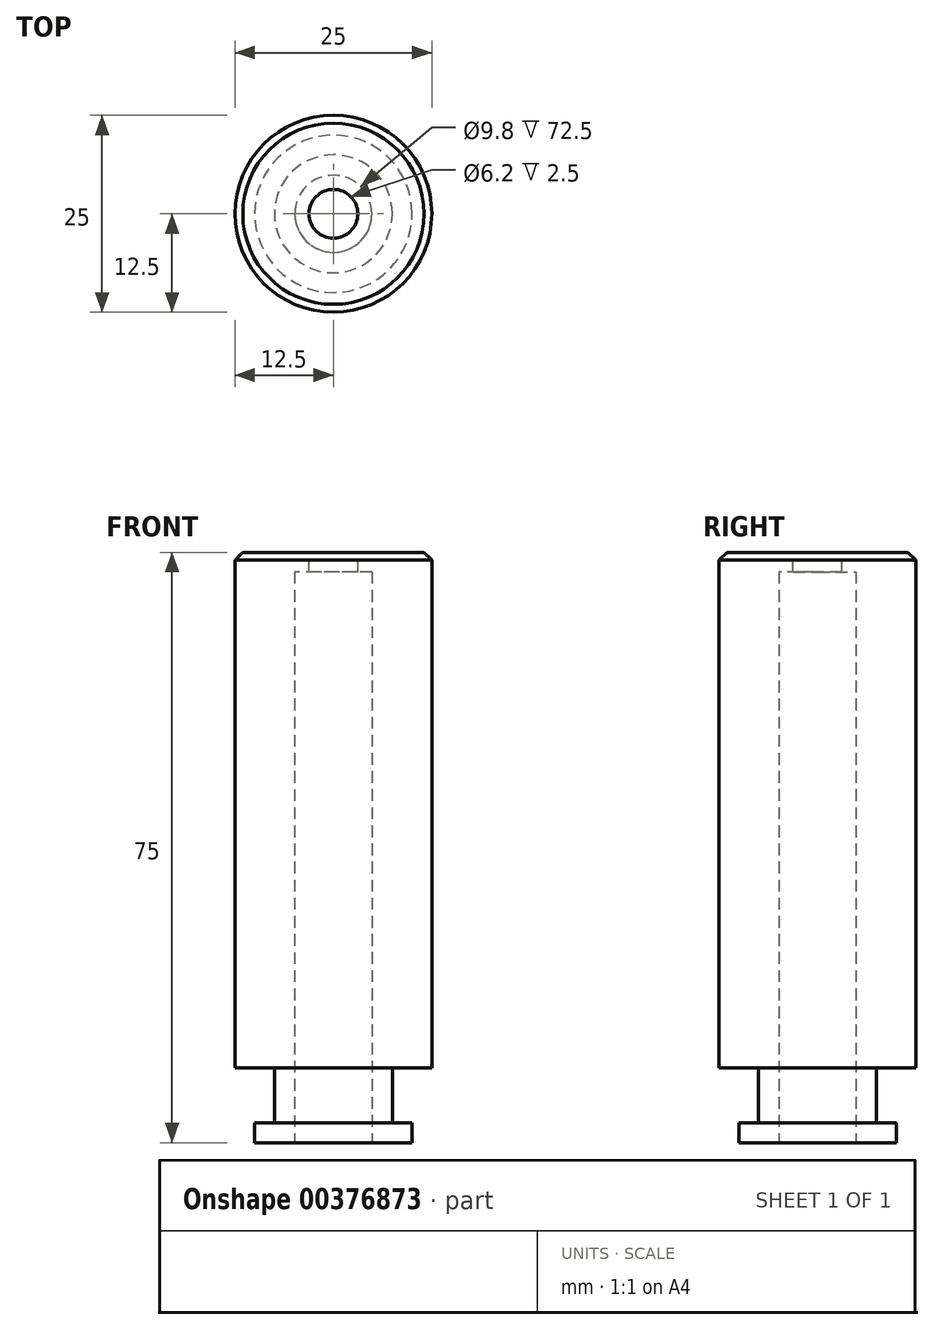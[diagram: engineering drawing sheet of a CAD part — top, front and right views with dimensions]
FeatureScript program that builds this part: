
annotation { "Feature Type Name" : "Feature", "Feature Type Description" : "" }
export const myFeature = defineFeature(function(context is Context, id is Id, definition is map)
    precondition{}
    {
        {
            var Q0;
            Q0=qCreatedBy(makeId("Top.planeOp"),FACE);
            var sketch = newSketch(context, id + "F0", { "sketchPlane" : qUnion([Q0])});
            skCircle(sketch, "E0", {"center": v(0, 0) * mm, "radius": 21.5 * mm});
            skSolve(sketch);
        }
        {
            var Q0;
            Q0=makeQuery(id+"F0.imprint","IMPRINT",FACE,{"disambiguationData":[TD([[makeQuery(id+"F0.imprint","IMPRINT",EDGE,{"derivedFrom":sQuery(id+"F0.wireOp",EDGE,"E0")}),1.0]])]});
            extrude(context, id + "F1", {"entities" : qUnion([Q0]), "depth" : 40 * mm});
        }
        {
            var Q0;
            Q0=makeQuery(id+"F1.opExtrude","CAP_EDGE",EDGE,{"disambiguationData":[OSD([sQuery(id+"F0.wireOp",EDGE,"E0")])],"isStart":false});
            fillet(context, id + "F2", {"entities" : qUnion([Q0]), "radius" : 5 * mm, "tangentPropagation" : true, "allowEdgeOverflow" : false});
        }
        {
            var Q0;
            Q0=makeQuery(id+"F1.opExtrude","CAP_FACE",FACE,{"disambiguationData":[OSD([sQuery(id+"F0.wireOp",EDGE,"E0")])],"isStart":true});
            var sketch = newSketch(context, id + "F3", { "sketchPlane" : qUnion([Q0])});
            skCircle(sketch, "E1", {"center": v(0, 0) * mm, "radius": 21.5 * mm});
            skSolve(sketch);
        }
        {
            var Q0;
            Q0=makeQuery(id+"F3.imprint","IMPRINT",FACE,{"disambiguationData":[TD([[makeQuery(id+"F3.imprint","IMPRINT",EDGE,{"derivedFrom":sQuery(id+"F3.wireOp",EDGE,"E1")}),-1.0]])]});
            extrude(context, id + "F4", {"entities" : qUnion([Q0]), "operationType" : NewBodyOperationType.ADD, "depth" : 40 * mm});
        }
        {
            var Q0;
            Q0=makeQuery(id+"F4.opExtrude","CAP_EDGE",EDGE,{"disambiguationData":[OSD([sQuery(id+"F3.wireOp",EDGE,"E1")])],"isStart":false});
            chamfer(context, id + "F5", {"entities" : qUnion([Q0]), "chamferType" : ChamferType.TWO_OFFSETS, "width1" : 40 * mm, "oppositeDirection" : false, "width2" : 7.5 * mm, "tangentPropagation" : true});
        }
        {
            var Q0;
            Q0=makeQuery(id+"F4.opExtrude","CAP_FACE",FACE,{"disambiguationData":[OSD([sQuery(id+"F3.wireOp",EDGE,"E1")])],"isStart":false});
            extrude(context, id + "F6", {"entities" : qUnion([Q0]), "operationType" : NewBodyOperationType.ADD, "depth" : 10 * mm});
        }
        {
            var Q0;
            {var subQ0=sQuery(id+"F3.wireOp",EDGE,"E1");Q0=makeQuery(id+"F5.opChamfer","BLEND_EDGE",EDGE,{"blendedFrom":[makeQuery(id+"F4.opExtrude","CAP_EDGE",EDGE,{"disambiguationData":[OSD([subQ0])],"isStart":false}),makeQuery(id+"F4.boolean.opBoolean","MERGE",FACE,{"derivedFrom":[makeQuery(id+"F1.opExtrude","SWEPT_FACE",FACE,{"disambiguationData":[OSD([sQuery(id+"F0.wireOp",EDGE,"E0")])]}),makeQuery(id+"F4.opExtrude","SWEPT_FACE",FACE,{"disambiguationData":[OSD([subQ0])]})]})],"blendedInto":[makeQuery(id+"F4.boolean.opBoolean","MERGE",FACE,{"derivedFrom":[makeQuery(id+"F1.opExtrude","SWEPT_FACE",FACE,{"disambiguationData":[OSD([sQuery(id+"F0.wireOp",EDGE,"E0")])]}),makeQuery(id+"F4.opExtrude","SWEPT_FACE",FACE,{"disambiguationData":[OSD([subQ0])]})]})]});}
            fillet(context, id + "F7", {"entities" : qUnion([Q0]), "radius" : 10 * mm, "tangentPropagation" : true, "allowEdgeOverflow" : false});
        }
        {
            var Q0;
            Q0=qCreatedBy(makeId("Right.planeOp"),FACE);
            var sketch = newSketch(context, id + "F8", { "sketchPlane" : qUnion([Q0])});
            skLineSegment(sketch, "E2.bottom", {"start": v(-17.43, -40.5) * mm, "end": v(-7.5, -40.5) * mm});
            skLineSegment(sketch, "E2.top", {"start": v(-10, -47.5) * mm, "end": v(-7.5, -47.5) * mm});
            skLineSegment(sketch, "E2.left", {"start": v(-17.43, -40.5) * mm, "end": v(-17.43, -47.5) * mm});
            skLineSegment(sketch, "E2.right", {"start": v(-7.5, -40.5) * mm, "end": v(-7.5, -47.5) * mm});
            skLineSegment(sketch, "E3", {"start": v(0, -39.98) * mm, "end": v(0, -66.82) * mm, "construction": true});
            skPoint(sketch, "E4.oppositeSnap0", {"position": v(-17.43, -44) * mm});
            skLineSegment(sketch, "E4.top", {"start": v(-10, -53.66) * mm, "end": v(-17.43, -53.66) * mm});
            skLineSegment(sketch, "E4.left", {"start": v(-10, -47.5) * mm, "end": v(-10, -53.66) * mm});
            skLineSegment(sketch, "E4.right", {"start": v(-17.43, -47.5) * mm, "end": v(-17.43, -53.66) * mm});
            skSolve(sketch);
        }
        {
            var Q0;
            Q0=makeQuery(id+"F8.imprint","IMPRINT",FACE,{"disambiguationData":[TD([[makeQuery(id+"F8.imprint","IMPRINT",EDGE,{"derivedFrom":sQuery(id+"F8.wireOp",EDGE,"E2.bottom")}),-1.0]])]});
            var Q1;
            Q1=sQuery(id+"F8.wireOp",EDGE,"E3");
            revolve(context, id + "F9", {"operationType" : NewBodyOperationType.REMOVE, "entities" : qUnion([Q0]), "axis" : qUnion([Q1]), "revolveType" : RevolveType.FULL, "oppositeDirection" : true});
        }
        {
            var Q0;
            Q0=makeQuery(id+"F6.opExtrude","CAP_FACE",FACE,{"disambiguationData":[OSD([sQuery(id+"F3.wireOp",EDGE,"E1")])],"isStart":false});
            var sketch = newSketch(context, id + "F10", { "sketchPlane" : qUnion([Q0])});
            skCircle(sketch, "E5", {"center": v(0, 0) * mm, "radius": 4.9 * mm});
            skSolve(sketch);
        }
        {
            var Q0;
            Q0=makeQuery(id+"F10.imprint","IMPRINT",FACE,{"disambiguationData":[TD([[makeQuery(id+"F10.imprint","IMPRINT",EDGE,{"derivedFrom":sQuery(id+"F10.wireOp",EDGE,"E5")}),1.0]])]});
            extrude(context, id + "F11", {"entities" : qUnion([Q0]), "operationType" : NewBodyOperationType.REMOVE, "oppositeDirection" : true, "depth" : 75 * mm});
        }
        {
            var Q0;
            Q0=makeQuery(id+"F1.opExtrude","CAP_FACE",FACE,{"disambiguationData":[OSD([sQuery(id+"F0.wireOp",EDGE,"E0")])],"isStart":false});
            var sketch = newSketch(context, id + "F12", { "sketchPlane" : qUnion([Q0])});
            skCircle(sketch, "E6", {"center": v(0, 0) * mm, "radius": 16.5 * mm});
            skSolve(sketch);
        }
        {
            var Q0;
            Q0=makeQuery(id+"F12.imprint","IMPRINT",FACE,{"disambiguationData":[TD([[makeQuery(id+"F12.imprint","IMPRINT",EDGE,{"derivedFrom":sQuery(id+"F12.wireOp",EDGE,"E6")}),1.0]])]});
            extrude(context, id + "F13", {"entities" : qUnion([Q0]), "operationType" : NewBodyOperationType.REMOVE, "oppositeDirection" : true, "depth" : 5 * mm});
        }
        {
            var Q0;
            Q0=makeQuery(id+"F13.boolean.opBoolean","COPY",FACE,{"derivedFrom":makeQuery(id+"F13.opExtrude","CAP_FACE",FACE,{"disambiguationData":[OSD([sQuery(id+"F12.wireOp",EDGE,"E6")])],"isStart":false})});
            var sketch = newSketch(context, id + "F14", { "sketchPlane" : qUnion([Q0])});
            skCircle(sketch, "E7", {"center": v(0, 0) * mm, "radius": 3.1 * mm});
            skSolve(sketch);
        }
        {
            var Q0;
            Q0=makeQuery(id+"F14.imprint","IMPRINT",FACE,{"disambiguationData":[TD([[makeQuery(id+"F14.imprint","IMPRINT",EDGE,{"derivedFrom":sQuery(id+"F14.wireOp",EDGE,"E7")}),1.0]])]});
            extrude(context, id + "F15", {"entities" : qUnion([Q0]), "operationType" : NewBodyOperationType.REMOVE, "endBound" : BoundingType.THROUGH_ALL, "oppositeDirection" : true, "depth" : 25 * mm});
        }
        {
            var Q0;
            Q0=makeQuery(id+"F6.opExtrude","CAP_FACE",FACE,{"disambiguationData":[OSD([sQuery(id+"F3.wireOp",EDGE,"E1")])],"isStart":false});
            var sketch = newSketch(context, id + "F16", { "sketchPlane" : qUnion([Q0])});
            skCircle(sketch, "E8", {"center": v(0, 0) * mm, "radius": 12.5 * mm});
            skCircle(sketch, "E9", {"center": v(0, 0) * mm, "radius": 45.5 * mm});
            skSolve(sketch);
        }
        {
            var Q0;
            Q0=makeQuery(id+"F16.imprint","IMPRINT",FACE,{"disambiguationData":[TD([[makeQuery(id+"F16.imprint","IMPRINT",EDGE,{"derivedFrom":sQuery(id+"F16.wireOp",EDGE,"E8")}),-1.0]])]});
            extrude(context, id + "F17", {"entities" : qUnion([Q0]), "operationType" : NewBodyOperationType.REMOVE, "oppositeDirection" : true, "depth" : 100 * mm});
        }
        {
            var Q0;
            Q0=qCreatedBy(makeId("Front.planeOp"),FACE);
            var sketch = newSketch(context, id + "F18", { "sketchPlane" : qUnion([Q0])});
            skLineSegment(sketch, "E10.bottom", {"start": v(-41.46, 68.36) * mm, "end": v(44.98, 68.36) * mm});
            skLineSegment(sketch, "E10.top", {"start": v(-41.46, 25) * mm, "end": v(44.98, 25) * mm});
            skLineSegment(sketch, "E10.left", {"start": v(-41.46, 68.36) * mm, "end": v(-41.46, 25) * mm});
            skLineSegment(sketch, "E10.right", {"start": v(44.98, 68.36) * mm, "end": v(44.98, 25) * mm});
            skSolve(sketch);
        }
        {
            var Q0;
            Q0=makeQuery(id+"F18.imprint","IMPRINT",FACE,{"disambiguationData":[TD([[makeQuery(id+"F18.imprint","IMPRINT",EDGE,{"derivedFrom":sQuery(id+"F18.wireOp",EDGE,"E10.bottom")}),-1.0]])]});
            extrude(context, id + "F19", {"entities" : qUnion([Q0]), "operationType" : NewBodyOperationType.REMOVE, "endBound" : BoundingType.SYMMETRIC, "oppositeDirection" : true, "depth" : 50 * mm});
        }
        {
            var Q0;
            Q0=makeQuery(id+"F19.boolean.opBoolean","INTERSECT",EDGE,{"derivedFrom":[makeQuery(id+"F17.boolean.opBoolean","COPY",FACE,{"derivedFrom":makeQuery(id+"F17.opExtrude","SWEPT_FACE",FACE,{"disambiguationData":[OSD([sQuery(id+"F16.wireOp",EDGE,"E8")])]})}),makeQuery(id+"F19.opExtrude","SWEPT_FACE",FACE,{"disambiguationData":[OSD([sQuery(id+"F18.wireOp",EDGE,"E10.top")])]})]});
            chamfer(context, id + "F20", {"entities" : qUnion([Q0]), "width" : 1 * mm, "tangentPropagation" : true});
        }
        {
            var Q0;
            Q0=makeQuery(id+"F19.boolean.opBoolean","COPY",FACE,{"derivedFrom":makeQuery(id+"F19.opExtrude","SWEPT_FACE",FACE,{"disambiguationData":[OSD([sQuery(id+"F18.wireOp",EDGE,"E10.top")])]})});
            var sketch = newSketch(context, id + "F21", { "sketchPlane" : qUnion([Q0])});
            skCircle(sketch, "E11", {"center": v(0, 0) * mm, "radius": 6.53 * mm});
            skCircle(sketch, "E12", {"center": v(0, 0) * mm, "radius": 3.1 * mm});
            skSolve(sketch);
        }
        {
            var Q0;
            Q0=makeQuery(id+"F21.imprint","IMPRINT",FACE,{"disambiguationData":[TD([[makeQuery(id+"F21.imprint","IMPRINT",EDGE,{"derivedFrom":sQuery(id+"F21.wireOp",EDGE,"E12")}),-1.0]])]});
            extrude(context, id + "F22", {"entities" : qUnion([Q0]), "operationType" : NewBodyOperationType.ADD, "oppositeDirection" : true, "depth" : 2.5 * mm});
        }
    });
